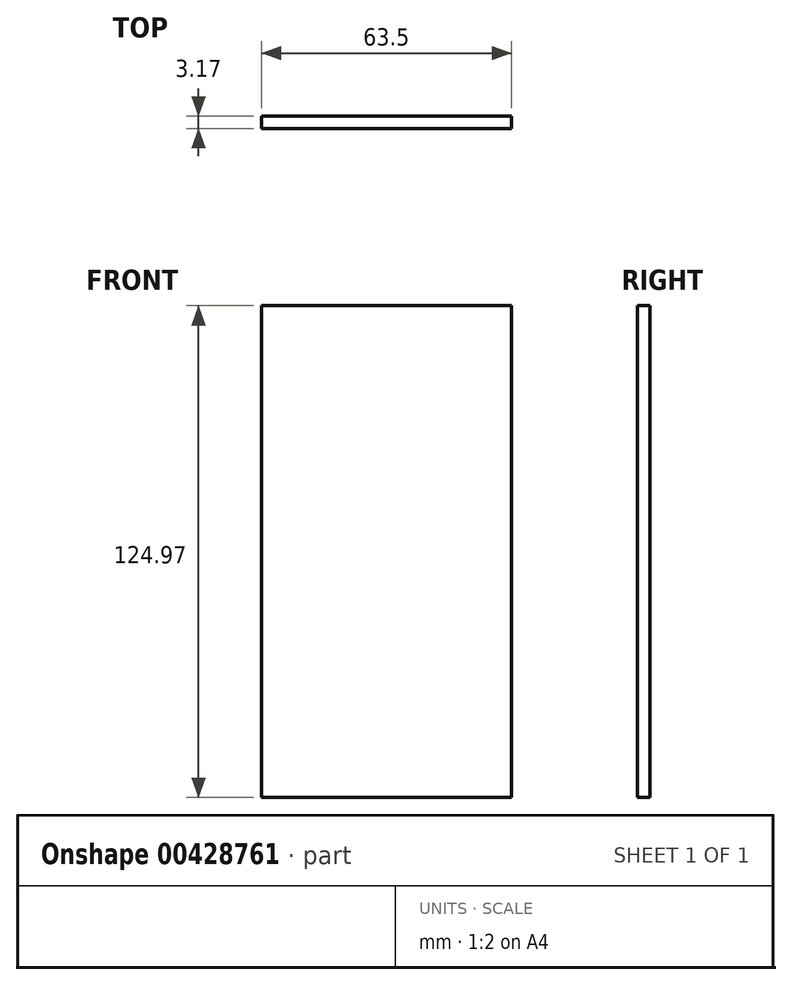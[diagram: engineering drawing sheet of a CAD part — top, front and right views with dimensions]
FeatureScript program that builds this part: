
annotation { "Feature Type Name" : "Feature", "Feature Type Description" : "" }
export const myFeature = defineFeature(function(context is Context, id is Id, definition is map)
    precondition{}
    {
        {
            var Q0;
            Q0=qCreatedBy(makeId("Front.planeOp"),FACE);
            var sketch = newSketch(context, id + "F0", { "sketchPlane" : qUnion([Q0])});
            skLineSegment(sketch, "E0.bottom", {"start": v(0, 0) * mm, "end": v(63.5, 0) * mm});
            skLineSegment(sketch, "E0.top", {"start": v(0, -124.97) * mm, "end": v(63.5, -124.97) * mm});
            skLineSegment(sketch, "E0.left", {"start": v(0, 0) * mm, "end": v(0, -124.97) * mm});
            skLineSegment(sketch, "E0.right", {"start": v(63.5, 0) * mm, "end": v(63.5, -124.97) * mm});
            skSolve(sketch);
        }
        {
            var Q0;
            Q0 = qSketchRegion(id + "F0", true);
            extrude(context, id + "F1", {"entities" : qUnion([Q0]), "depth" : 3.17 * mm});
        }
    });
